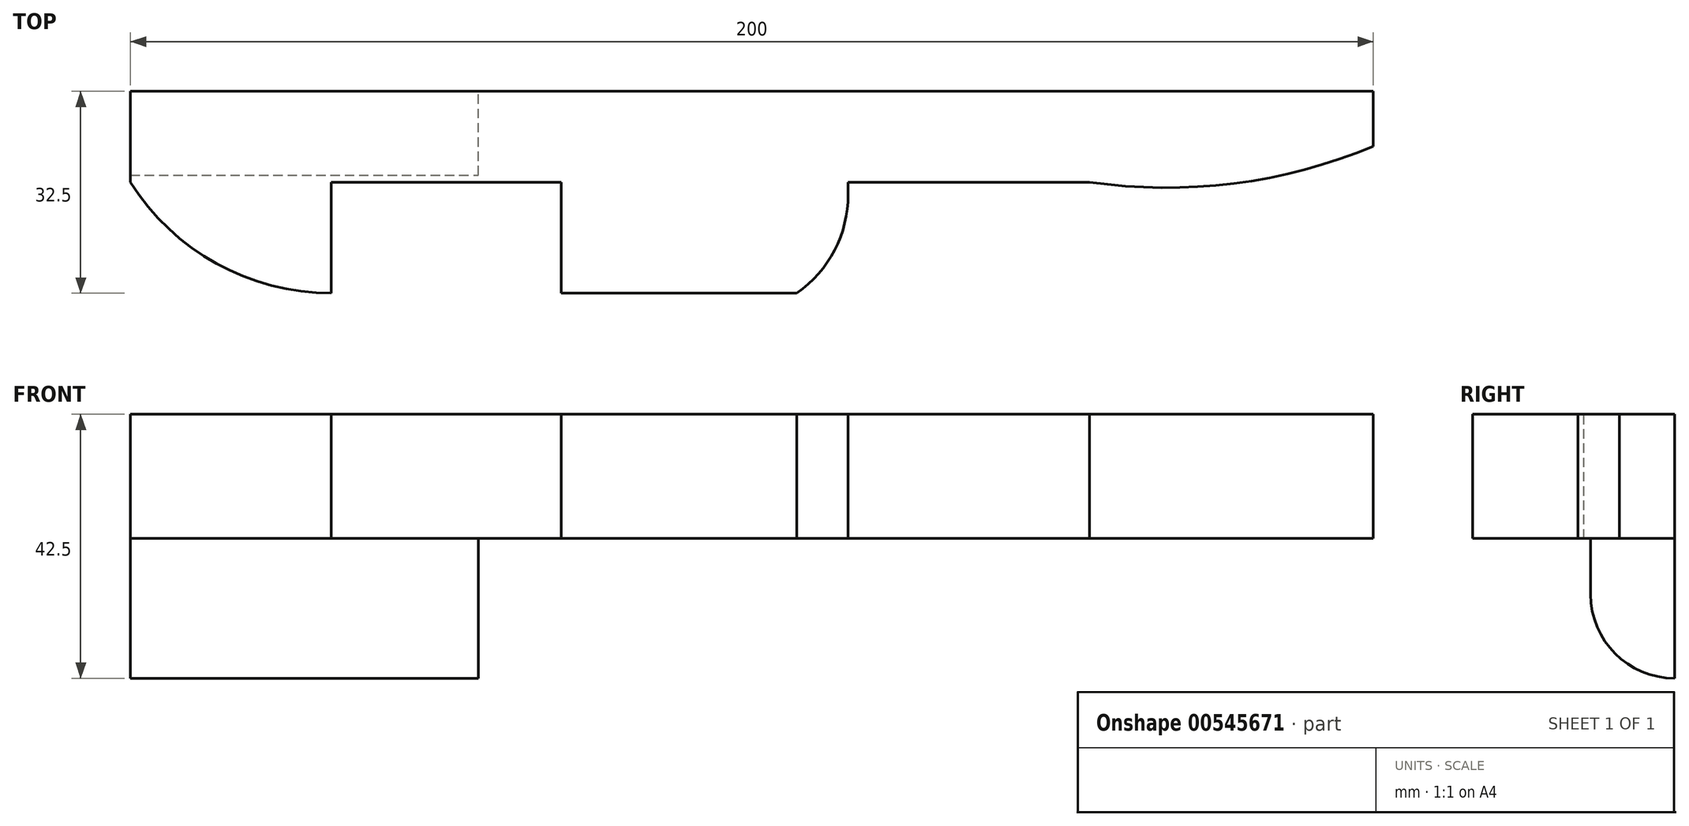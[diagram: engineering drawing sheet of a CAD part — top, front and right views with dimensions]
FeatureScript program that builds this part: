
annotation { "Feature Type Name" : "Feature", "Feature Type Description" : "" }
export const myFeature = defineFeature(function(context is Context, id is Id, definition is map)
    precondition{}
    {
        {
            var Q0;
            Q0=qCreatedBy(makeId("Top.planeOp"),FACE);
            var sketch = newSketch(context, id + "F0", { "sketchPlane" : qUnion([Q0])});
            skLineSegment(sketch, "E0.bottom", {"start": v(0, -32.5) * mm, "end": v(200, -32.5) * mm, "construction": true});
            skLineSegment(sketch, "E0.top", {"start": v(0, 32.5) * mm, "end": v(200, 32.5) * mm, "construction": true});
            skLineSegment(sketch, "E0.left", {"start": v(0, -32.5) * mm, "end": v(0, 32.5) * mm, "construction": true});
            skLineSegment(sketch, "E0.right", {"start": v(200, -32.5) * mm, "end": v(200, 32.5) * mm, "construction": true});
            skLineSegment(sketch, "E1", {"start": v(0, 0) * mm, "end": v(200, 0) * mm});
            skLineSegment(sketch, "E2.bottom", {"start": v(34.3, -32.5) * mm, "end": v(67.3, -32.5) * mm});
            skLineSegment(sketch, "E2.top", {"start": v(34.3, -16.6) * mm, "end": v(67.3, -16.6) * mm});
            skLineSegment(sketch, "E2.left", {"start": v(34.3, -32.5) * mm, "end": v(34.3, -16.61) * mm});
            skLineSegment(sketch, "E2.right", {"start": v(67.3, -32.5) * mm, "end": v(67.3, -16.6) * mm});
            skLineSegment(sketch, "E3.bottom", {"start": v(130.5, -16.6) * mm, "end": v(163.5, -16.6) * mm});
            skLineSegment(sketch, "E3.top", {"start": v(130.5, -32.5) * mm, "end": v(163.5, -32.5) * mm});
            skLineSegment(sketch, "E3.left", {"start": v(130.5, -16.6) * mm, "end": v(130.5, -32.5) * mm});
            skLineSegment(sketch, "E3.right", {"start": v(163.5, -16.6) * mm, "end": v(163.5, -32.5) * mm});
            skLineSegment(sketch, "E4", {"start": v(32.3, -32.5) * mm, "end": v(32.3, -14.61) * mm});
            skLineSegment(sketch, "E5", {"start": v(32.3, -14.61) * mm, "end": v(69.3, -14.61) * mm});
            skLineSegment(sketch, "E6", {"start": v(69.3, -14.61) * mm, "end": v(69.3, -32.5) * mm});
            skLineSegment(sketch, "E7.bottom", {"start": v(130.5, -16.6) * mm, "end": v(115.5, -16.6) * mm});
            skLineSegment(sketch, "E7.top", {"start": v(130.5, -32.5) * mm, "end": v(115.5, -32.5) * mm});
            skLineSegment(sketch, "E7.right", {"start": v(115.5, -16.6) * mm, "end": v(115.5, -32.5) * mm});
            skLineSegment(sketch, "E8", {"start": v(69.3, -32.5) * mm, "end": v(107.26, -32.5) * mm});
            skLineSegment(sketch, "E9", {"start": v(115.5, -16.6) * mm, "end": v(115.5, -14.61) * mm});
            skLineSegment(sketch, "E10", {"start": v(115.5, -14.61) * mm, "end": v(154.34, -14.6) * mm});
            skArc(sketch, "E11", {"start": v(154.34, -14.61) * mm, "mid": v(177.56, -14.83) * mm, "end": v(200, -8.86) * mm});
            skArc(sketch, "E12", {"start": v(0, -14.61) * mm, "mid": v(13.84, -27.73) * mm, "end": v(32.3, -32.5) * mm});
            skArc(sketch, "E13", {"start": v(107.26, -32.5) * mm, "mid": v(113.32, -25.56) * mm, "end": v(115.5, -16.6) * mm});
            skLineSegment(sketch, "E14", {"start": v(200, -8.86) * mm, "end": v(200, 0) * mm});
            skLineSegment(sketch, "E15", {"start": v(200, 0) * mm, "end": v(0, 0) * mm});
            skLineSegment(sketch, "E16", {"start": v(0, -14.61) * mm, "end": v(0, 0) * mm});
            skSolve(sketch);
        }
        {
            var Q0;
            Q0=qCreatedBy(makeId("Right.planeOp"),FACE);
            var sketch = newSketch(context, id + "F1", { "sketchPlane" : qUnion([Q0])});
            skLineSegment(sketch, "E17.0", {"start": v(-32.5, 0) * mm, "end": v(32.5, 0) * mm, "construction": true});
            skLineSegment(sketch, "E18", {"start": v(32.5, 0) * mm, "end": v(32.5, -50) * mm, "construction": true});
            skLineSegment(sketch, "E19", {"start": v(32.5, -50) * mm, "end": v(-32.5, -50) * mm, "construction": true});
            skLineSegment(sketch, "E20", {"start": v(-32.5, -50) * mm, "end": v(-32.5, 0) * mm, "construction": true});
            skLineSegment(sketch, "E21", {"start": v(0, 0) * mm, "end": v(0, -50) * mm});
            skArc(sketch, "E22", {"start": v(0, -19.5) * mm, "mid": v(-9.5, -29) * mm, "end": v(0, -38.5) * mm});
            skLineSegment(sketch, "E23", {"start": v(0, -6) * mm, "end": v(-6, -6) * mm});
            skLineSegment(sketch, "E24", {"start": v(-6, -6) * mm, "end": v(-6, 0) * mm});
            skArc(sketch, "E25", {"start": v(-13.5, -29) * mm, "mid": v(-9.55, -38.55) * mm, "end": v(0, -42.5) * mm});
            skLineSegment(sketch, "E26", {"start": v(-13.5, -29) * mm, "end": v(-13.5, -11.71) * mm});
            skLineSegment(sketch, "E27", {"start": v(-13.5, -11.71) * mm, "end": v(0, -11.71) * mm});
            skSolve(sketch);
        }
        {
            var Q0;
            Q0=makeQuery(id+"F0.imprint","IMPRINT",FACE,{"disambiguationData":[TD([[makeQuery(id+"F0.imprint","IMPRINT",EDGE,{"derivedFrom":sQuery(id+"F0.wireOp",EDGE,"E1")}),-1.0]])]});
            extrude(context, id + "F2", {"entities" : qUnion([Q0]), "oppositeDirection" : true, "depth" : 20 * mm, "offsetDistance" : 25 * mm});
        }
        {
            var Q0;
            {var subQ0=sQuery(id+"F1.wireOp",EDGE,"E22");Q0=makeQuery(id+"F1.imprint","IMPRINT",FACE,{"disambiguationData":[TD([[makeQuery(id+"F1.imprint","IMPRINT",EDGE,{"derivedFrom":subQ0}),1.0]])]});}
            var Q1;
            {var subQ1=sQuery(id+"F1.wireOp",EDGE,"E22");Q1=makeQuery(id+"F1.imprint","IMPRINT",FACE,{"disambiguationData":[TD([[makeQuery(id+"F1.imprint","IMPRINT",EDGE,{"derivedFrom":subQ1}),-1.0]])]});}
            extrude(context, id + "F3", {"entities" : qUnion([Q0, Q1]), "operationType" : NewBodyOperationType.ADD, "depth" : 56 * mm, "offsetDistance" : 25 * mm});
        }
        {
            var Q0;
            {var subQ0=sQuery(id+"F1.wireOp",EDGE,"E22");Q0=makeQuery(id+"F1.imprint","IMPRINT",FACE,{"disambiguationData":[TD([[makeQuery(id+"F1.imprint","IMPRINT",EDGE,{"derivedFrom":subQ0}),1.0]])]});}
            extrude(context, id + "F4", {"entities" : qUnion([Q0]), "operationType" : NewBodyOperationType.REMOVE, "oppositeDirection" : true, "depth" : 52 * mm, "offsetDistance" : 25 * mm});
        }
    });
